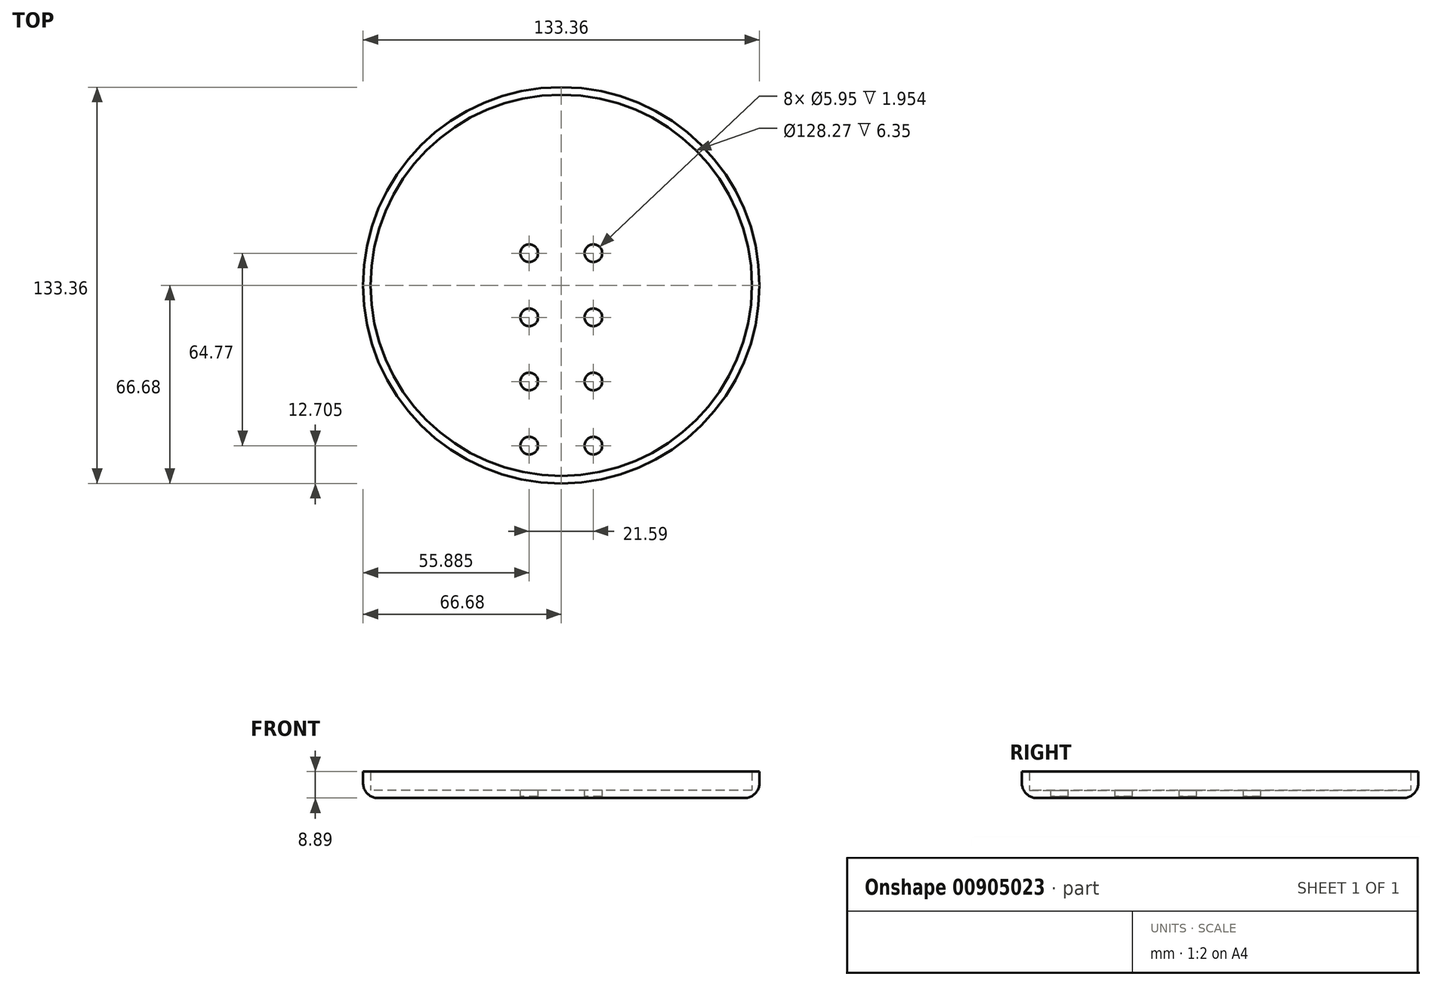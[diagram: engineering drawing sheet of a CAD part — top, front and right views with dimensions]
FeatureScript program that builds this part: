
annotation { "Feature Type Name" : "Feature", "Feature Type Description" : "" }
export const myFeature = defineFeature(function(context is Context, id is Id, definition is map)
    precondition{}
    {
        {
            var Q0;
            Q0=qCreatedBy(makeId("Top.planeOp"),FACE);
            var sketch = newSketch(context, id + "F0", { "sketchPlane" : qUnion([Q0])});
            skCircle(sketch, "E0", {"center": v(0, 0) * mm, "radius": 66.68 * mm});
            skSolve(sketch);
        }
        {
            var Q0;
            Q0 = qSketchRegion(id + "F0", true);
            extrude(context, id + "F1", {"entities" : qUnion([Q0]), "depth" : 2.54 * mm, "offsetDistance" : 25.4 * mm});
        }
        {
            var Q0;
            Q0=makeQuery(id+"F1.opExtrude","CAP_FACE",FACE,{"disambiguationData":[OSD([sQuery(id+"F0.wireOp",EDGE,"E0")])],"isStart":false});
            var sketch = newSketch(context, id + "F2", { "sketchPlane" : qUnion([Q0])});
            skCircle(sketch, "E1.0", {"center": v(0, 0) * mm, "radius": 64.14 * mm});
            skSolve(sketch);
        }
        {
            var Q0;
            Q0=makeQuery(id+"F2.imprint","IMPRINT",FACE,{"disambiguationData":[TD([[makeQuery(id+"F2.imprint","IMPRINT",EDGE,{"derivedFrom":sQuery(id+"F2.wireOp",EDGE,"E1.0")}),-1.0]])]});
            extrude(context, id + "F3", {"entities" : qUnion([Q0]), "operationType" : NewBodyOperationType.ADD, "depth" : 6.35 * mm, "offsetDistance" : 25.4 * mm});
        }
        {
            var Q0;
            Q0=makeQuery(id+"F3.opExtrude","CAP_EDGE",EDGE,{"disambiguationData":[OSD([sQuery(id+"F2.wireOp",EDGE,"E1.0")])],"isStart":true});
            var Q1;
            Q1=makeQuery(id+"F1.opExtrude","CAP_EDGE",EDGE,{"disambiguationData":[OSD([sQuery(id+"F0.wireOp",EDGE,"E0")])],"isStart":true});
            fillet(context, id + "F4", {"entities" : qUnion([Q0, Q1]), "radius" : 5.08 * mm, "tangentPropagation" : true, "allowEdgeOverflow" : false});
        }
        {
            var Q0;
            Q0=makeQuery(id+"F1.opExtrude","CAP_FACE",FACE,{"disambiguationData":[OSD([sQuery(id+"F0.wireOp",EDGE,"E0")])],"isStart":false});
            var sketch = newSketch(context, id + "F5", { "sketchPlane" : qUnion([Q0])});
            skLineSegment(sketch, "E2.bottom", {"start": v(10.8, 10.8) * mm, "end": v(-10.8, 10.8) * mm});
            skLineSegment(sketch, "E2.top", {"start": v(10.8, -10.8) * mm, "end": v(-10.8, -10.8) * mm});
            skLineSegment(sketch, "E2.left", {"start": v(10.8, 10.8) * mm, "end": v(10.8, -10.8) * mm});
            skLineSegment(sketch, "E2.right", {"start": v(-10.8, 10.8) * mm, "end": v(-10.8, -10.8) * mm});
            skPoint(sketch, "E2.middle", {"position": v(0, 0) * mm});
            skLineSegment(sketch, "E3.bottom", {"start": v(10.8, -32.39) * mm, "end": v(-10.8, -32.39) * mm});
            skLineSegment(sketch, "E3.top", {"start": v(10.8, -53.98) * mm, "end": v(-10.8, -53.98) * mm});
            skLineSegment(sketch, "E3.left", {"start": v(10.8, -32.39) * mm, "end": v(10.8, -53.98) * mm});
            skLineSegment(sketch, "E3.right", {"start": v(-10.8, -32.39) * mm, "end": v(-10.8, -53.98) * mm});
            skPoint(sketch, "E3.middle", {"position": v(0, -43.18) * mm});
            skCircle(sketch, "E4", {"center": v(-10.8, 10.8) * mm, "radius": 2.98 * mm});
            skCircle(sketch, "E5", {"center": v(10.8, 10.8) * mm, "radius": 2.98 * mm});
            skCircle(sketch, "E6", {"center": v(10.8, -10.8) * mm, "radius": 2.98 * mm});
            skCircle(sketch, "E7", {"center": v(-10.8, -10.8) * mm, "radius": 2.98 * mm});
            skCircle(sketch, "E8", {"center": v(-10.8, -32.39) * mm, "radius": 2.98 * mm});
            skCircle(sketch, "E9", {"center": v(10.8, -32.39) * mm, "radius": 2.98 * mm});
            skCircle(sketch, "E10", {"center": v(10.8, -53.98) * mm, "radius": 2.98 * mm});
            skCircle(sketch, "E11", {"center": v(-10.8, -53.98) * mm, "radius": 2.98 * mm});
            skSolve(sketch);
        }
        {
            var Q0;
            {var subQ0=sQuery(id+"F5.wireOp",EDGE,"E2.left");var subQ1=sQuery(id+"F5.wireOp",EDGE,"E2.bottom");var subQ2=makeQuery(id+"F5.imprint","INTERSECT",VERTEX,{"derivedFrom":[subQ1,subQ0]});Q0=makeQuery(id+"F5.imprint","IMPRINT",FACE,{"disambiguationData":[TD([[makeQuery(id+"F5.imprint","IMPRINT",EDGE,{"disambiguationData":[TD([[subQ2,-1.0]])],"derivedFrom":subQ1}),1.0]])]});}
            var Q1;
            {var subQ0=sQuery(id+"F5.wireOp",EDGE,"E2.left");var subQ1=sQuery(id+"F5.wireOp",EDGE,"E2.bottom");var subQ2=makeQuery(id+"F5.imprint","INTERSECT",VERTEX,{"derivedFrom":[subQ1,subQ0]});Q1=makeQuery(id+"F5.imprint","IMPRINT",FACE,{"disambiguationData":[TD([[makeQuery(id+"F5.imprint","IMPRINT",EDGE,{"disambiguationData":[TD([[subQ2,-1.0]])],"derivedFrom":subQ1}),-1.0]])]});}
            var Q2;
            {var subQ0=sQuery(id+"F5.wireOp",EDGE,"E2.right");var subQ1=sQuery(id+"F5.wireOp",EDGE,"E2.bottom");var subQ2=makeQuery(id+"F5.imprint","INTERSECT",VERTEX,{"derivedFrom":[subQ1,subQ0]});Q2=makeQuery(id+"F5.imprint","IMPRINT",FACE,{"disambiguationData":[TD([[makeQuery(id+"F5.imprint","IMPRINT",EDGE,{"disambiguationData":[TD([[subQ2,1.0]])],"derivedFrom":subQ1}),-1.0]])]});}
            var Q3;
            {var subQ0=sQuery(id+"F5.wireOp",EDGE,"E2.right");var subQ1=sQuery(id+"F5.wireOp",EDGE,"E2.bottom");var subQ2=makeQuery(id+"F5.imprint","INTERSECT",VERTEX,{"derivedFrom":[subQ1,subQ0]});Q3=makeQuery(id+"F5.imprint","IMPRINT",FACE,{"disambiguationData":[TD([[makeQuery(id+"F5.imprint","IMPRINT",EDGE,{"disambiguationData":[TD([[subQ2,1.0]])],"derivedFrom":subQ1}),1.0]])]});}
            var Q4;
            {var subQ0=sQuery(id+"F5.wireOp",EDGE,"E2.left");var subQ1=sQuery(id+"F5.wireOp",EDGE,"E2.top");var subQ2=makeQuery(id+"F5.imprint","INTERSECT",VERTEX,{"derivedFrom":[subQ1,subQ0]});Q4=makeQuery(id+"F5.imprint","IMPRINT",FACE,{"disambiguationData":[TD([[makeQuery(id+"F5.imprint","IMPRINT",EDGE,{"disambiguationData":[TD([[subQ2,-1.0]])],"derivedFrom":subQ1}),-1.0]])]});}
            var Q5;
            {var subQ0=sQuery(id+"F5.wireOp",EDGE,"E2.left");var subQ1=sQuery(id+"F5.wireOp",EDGE,"E2.top");var subQ2=makeQuery(id+"F5.imprint","INTERSECT",VERTEX,{"derivedFrom":[subQ1,subQ0]});Q5=makeQuery(id+"F5.imprint","IMPRINT",FACE,{"disambiguationData":[TD([[makeQuery(id+"F5.imprint","IMPRINT",EDGE,{"disambiguationData":[TD([[subQ2,-1.0]])],"derivedFrom":subQ1}),1.0]])]});}
            var Q6;
            {var subQ0=sQuery(id+"F5.wireOp",EDGE,"E2.right");var subQ1=sQuery(id+"F5.wireOp",EDGE,"E2.top");var subQ2=makeQuery(id+"F5.imprint","INTERSECT",VERTEX,{"derivedFrom":[subQ1,subQ0]});Q6=makeQuery(id+"F5.imprint","IMPRINT",FACE,{"disambiguationData":[TD([[makeQuery(id+"F5.imprint","IMPRINT",EDGE,{"disambiguationData":[TD([[subQ2,1.0]])],"derivedFrom":subQ1}),-1.0]])]});}
            var Q7;
            {var subQ0=sQuery(id+"F5.wireOp",EDGE,"E2.right");var subQ1=sQuery(id+"F5.wireOp",EDGE,"E2.top");var subQ2=makeQuery(id+"F5.imprint","INTERSECT",VERTEX,{"derivedFrom":[subQ1,subQ0]});Q7=makeQuery(id+"F5.imprint","IMPRINT",FACE,{"disambiguationData":[TD([[makeQuery(id+"F5.imprint","IMPRINT",EDGE,{"disambiguationData":[TD([[subQ2,1.0]])],"derivedFrom":subQ1}),1.0]])]});}
            var Q8;
            {var subQ0=sQuery(id+"F5.wireOp",EDGE,"E3.left");var subQ1=sQuery(id+"F5.wireOp",EDGE,"E3.bottom");var subQ2=makeQuery(id+"F5.imprint","INTERSECT",VERTEX,{"derivedFrom":[subQ1,subQ0]});Q8=makeQuery(id+"F5.imprint","IMPRINT",FACE,{"disambiguationData":[TD([[makeQuery(id+"F5.imprint","IMPRINT",EDGE,{"disambiguationData":[TD([[subQ2,-1.0]])],"derivedFrom":subQ1}),1.0]])]});}
            var Q9;
            {var subQ0=sQuery(id+"F5.wireOp",EDGE,"E3.left");var subQ1=sQuery(id+"F5.wireOp",EDGE,"E3.bottom");var subQ2=makeQuery(id+"F5.imprint","INTERSECT",VERTEX,{"derivedFrom":[subQ1,subQ0]});Q9=makeQuery(id+"F5.imprint","IMPRINT",FACE,{"disambiguationData":[TD([[makeQuery(id+"F5.imprint","IMPRINT",EDGE,{"disambiguationData":[TD([[subQ2,-1.0]])],"derivedFrom":subQ1}),-1.0]])]});}
            var Q10;
            {var subQ0=sQuery(id+"F5.wireOp",EDGE,"E3.right");var subQ1=sQuery(id+"F5.wireOp",EDGE,"E3.bottom");var subQ2=makeQuery(id+"F5.imprint","INTERSECT",VERTEX,{"derivedFrom":[subQ1,subQ0]});Q10=makeQuery(id+"F5.imprint","IMPRINT",FACE,{"disambiguationData":[TD([[makeQuery(id+"F5.imprint","IMPRINT",EDGE,{"disambiguationData":[TD([[subQ2,1.0]])],"derivedFrom":subQ1}),-1.0]])]});}
            var Q11;
            {var subQ0=sQuery(id+"F5.wireOp",EDGE,"E3.right");var subQ1=sQuery(id+"F5.wireOp",EDGE,"E3.bottom");var subQ2=makeQuery(id+"F5.imprint","INTERSECT",VERTEX,{"derivedFrom":[subQ1,subQ0]});Q11=makeQuery(id+"F5.imprint","IMPRINT",FACE,{"disambiguationData":[TD([[makeQuery(id+"F5.imprint","IMPRINT",EDGE,{"disambiguationData":[TD([[subQ2,1.0]])],"derivedFrom":subQ1}),1.0]])]});}
            var Q12;
            {var subQ0=sQuery(id+"F5.wireOp",EDGE,"E3.left");var subQ1=sQuery(id+"F5.wireOp",EDGE,"E3.top");var subQ2=makeQuery(id+"F5.imprint","INTERSECT",VERTEX,{"derivedFrom":[subQ1,subQ0]});Q12=makeQuery(id+"F5.imprint","IMPRINT",FACE,{"disambiguationData":[TD([[makeQuery(id+"F5.imprint","IMPRINT",EDGE,{"disambiguationData":[TD([[subQ2,-1.0]])],"derivedFrom":subQ1}),1.0]])]});}
            var Q13;
            {var subQ0=sQuery(id+"F5.wireOp",EDGE,"E3.right");var subQ1=sQuery(id+"F5.wireOp",EDGE,"E3.top");var subQ2=makeQuery(id+"F5.imprint","INTERSECT",VERTEX,{"derivedFrom":[subQ1,subQ0]});Q13=makeQuery(id+"F5.imprint","IMPRINT",FACE,{"disambiguationData":[TD([[makeQuery(id+"F5.imprint","IMPRINT",EDGE,{"disambiguationData":[TD([[subQ2,1.0]])],"derivedFrom":subQ1}),1.0]])]});}
            var Q14;
            {var subQ0=sQuery(id+"F5.wireOp",EDGE,"E3.left");var subQ1=sQuery(id+"F5.wireOp",EDGE,"E3.top");var subQ2=makeQuery(id+"F5.imprint","INTERSECT",VERTEX,{"derivedFrom":[subQ1,subQ0]});Q14=makeQuery(id+"F5.imprint","IMPRINT",FACE,{"disambiguationData":[TD([[makeQuery(id+"F5.imprint","IMPRINT",EDGE,{"disambiguationData":[TD([[subQ2,-1.0]])],"derivedFrom":subQ1}),-1.0]])]});}
            var Q15;
            {var subQ0=sQuery(id+"F5.wireOp",EDGE,"E3.right");var subQ1=sQuery(id+"F5.wireOp",EDGE,"E3.top");var subQ2=makeQuery(id+"F5.imprint","INTERSECT",VERTEX,{"derivedFrom":[subQ1,subQ0]});Q15=makeQuery(id+"F5.imprint","IMPRINT",FACE,{"disambiguationData":[TD([[makeQuery(id+"F5.imprint","IMPRINT",EDGE,{"disambiguationData":[TD([[subQ2,1.0]])],"derivedFrom":subQ1}),-1.0]])]});}
            var Q16;
            {var subQ0=sQuery(id+"F5.wireOp",EDGE,"E10");var subQ1=sQuery(id+"F5.wireOp",EDGE,"E3.left");var subQ2=makeQuery(id+"F5.imprint","INTERSECT",VERTEX,{"derivedFrom":[subQ1,subQ0]});Q16=makeQuery(id+"F5.imprint","IMPRINT",FACE,{"disambiguationData":[TD([[makeQuery(id+"F5.imprint","IMPRINT",EDGE,{"disambiguationData":[TD([[subQ2,-1.0]])],"derivedFrom":subQ1}),1.0]])]});}
            var Q17;
            {var subQ0=sQuery(id+"F5.wireOp",EDGE,"E10");var subQ1=sQuery(id+"F5.wireOp",EDGE,"E3.left");var subQ2=makeQuery(id+"F5.imprint","INTERSECT",VERTEX,{"derivedFrom":[subQ1,subQ0]});Q17=makeQuery(id+"F5.imprint","IMPRINT",FACE,{"disambiguationData":[TD([[makeQuery(id+"F5.imprint","IMPRINT",EDGE,{"disambiguationData":[TD([[subQ2,-1.0]])],"derivedFrom":subQ1}),-1.0]])]});}
            var Q18;
            {var subQ0=sQuery(id+"F5.wireOp",EDGE,"E11");var subQ1=sQuery(id+"F5.wireOp",EDGE,"E3.right");var subQ2=makeQuery(id+"F5.imprint","INTERSECT",VERTEX,{"derivedFrom":[subQ1,subQ0]});Q18=makeQuery(id+"F5.imprint","IMPRINT",FACE,{"disambiguationData":[TD([[makeQuery(id+"F5.imprint","IMPRINT",EDGE,{"disambiguationData":[TD([[subQ2,-1.0]])],"derivedFrom":subQ1}),1.0]])]});}
            var Q19;
            {var subQ0=sQuery(id+"F5.wireOp",EDGE,"E11");var subQ1=sQuery(id+"F5.wireOp",EDGE,"E3.right");var subQ2=makeQuery(id+"F5.imprint","INTERSECT",VERTEX,{"derivedFrom":[subQ1,subQ0]});Q19=makeQuery(id+"F5.imprint","IMPRINT",FACE,{"disambiguationData":[TD([[makeQuery(id+"F5.imprint","IMPRINT",EDGE,{"disambiguationData":[TD([[subQ2,-1.0]])],"derivedFrom":subQ1}),-1.0]])]});}
            extrude(context, id + "F6", {"entities" : qUnion([Q0, Q1, Q2, Q3, Q4, Q5, Q6, Q7, Q8, Q9, Q10, Q11, Q12, Q13, Q14, Q15, Q16, Q17, Q18, Q19]), "operationType" : NewBodyOperationType.REMOVE, "oppositeDirection" : true, "depth" : 1.95 * mm, "offsetDistance" : 25.4 * mm});
        }
    });
